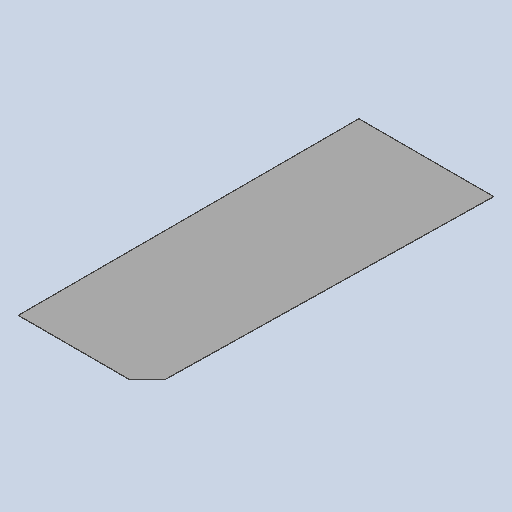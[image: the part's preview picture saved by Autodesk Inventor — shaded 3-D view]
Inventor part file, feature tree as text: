
AUTODESK INVENTOR PART (.ipt)
format: ipt  version: 2025 (Build 290162010, 162A)  size: 116,224 bytes
history: native  units: mm
features: other x3, sheet_metal_op x1, sketch x1
ambient origin geometry x8: Origin, YZ Plane, XZ Plane, XY Plane, X Axis, Y Axis, Z Axis, Center Point
bodies: Body1 (feature_tree)
feature tree (5):
  sheet_metal_op  "Face2"
  other  "Corner Chamfer1"
  sketch  "Sketch5"  dims[d26=1200.0mm d27=2897.0mm d28=3.0mm d29=53.0mm d30=947.0mm d31=150.0mm d32=103.0mm d33=6.0mm d34=6.0mm d35=45.0deg]
  other  "Plate4"
  other  "Definition1"
